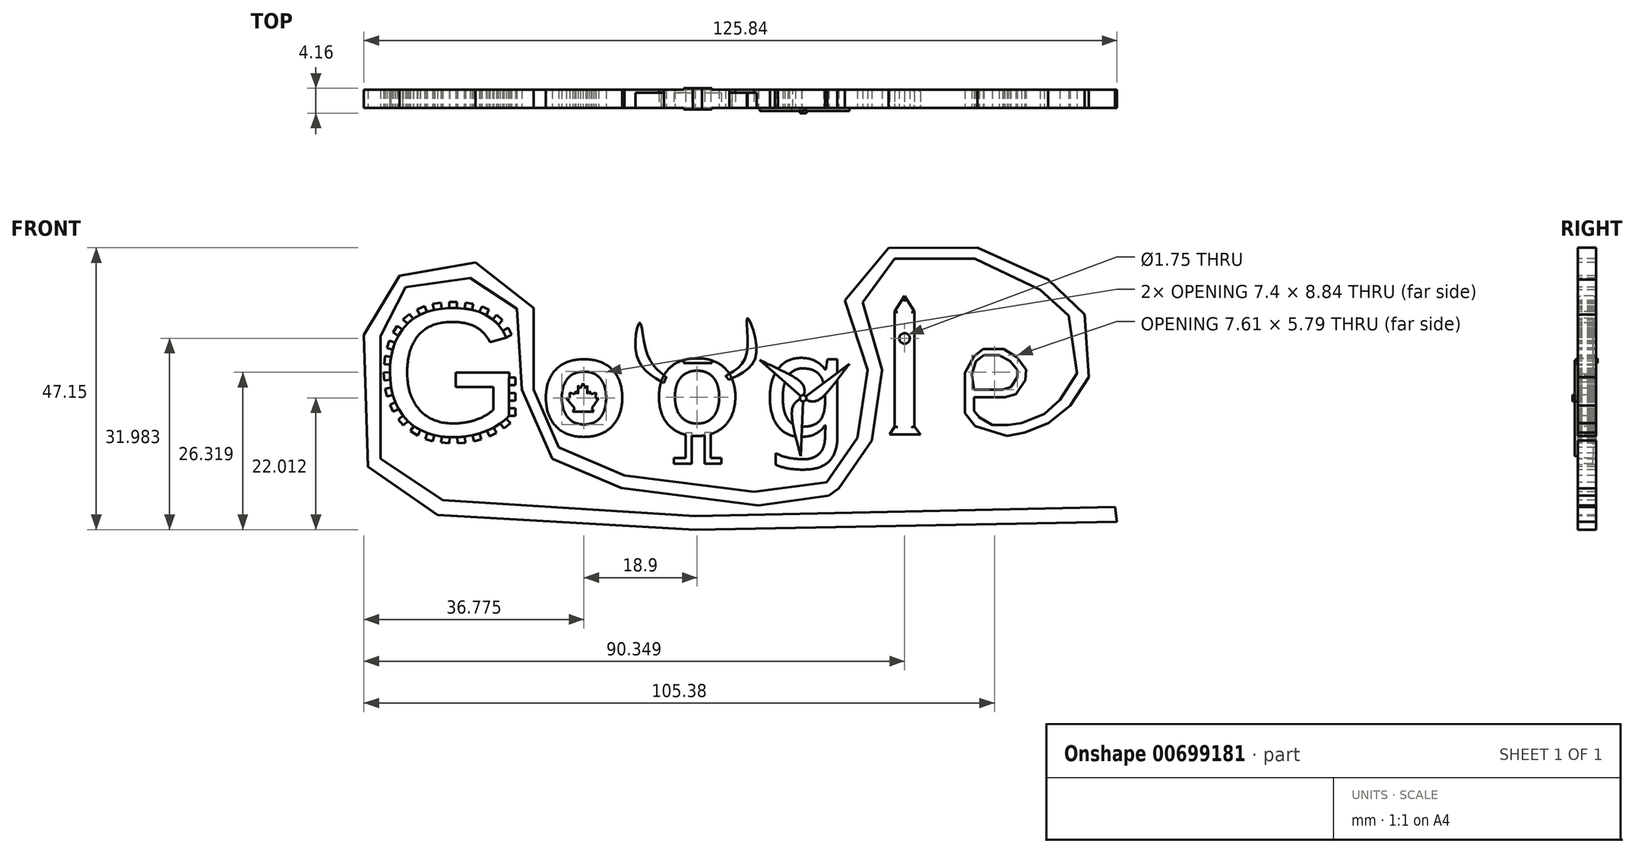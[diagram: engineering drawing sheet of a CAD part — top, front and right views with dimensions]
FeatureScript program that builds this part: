
annotation { "Feature Type Name" : "Feature", "Feature Type Description" : "" }
export const myFeature = defineFeature(function(context is Context, id is Id, definition is map)
    precondition{}
    {
        {
            var Q0;
            Q0=qCreatedBy(makeId("Front.planeOp"),FACE);
            var sketch = newSketch(context, id + "F0", { "sketchPlane" : qUnion([Q0])});
            skText(sketch, "E0", { "text": "G", "fontName": "Arimo-Regular.ttf"});
            skLineSegment(sketch, "E1", {"start": v(-51.76, 5.44) * mm, "end": v(-52.37, 6.57) * mm});
            skLineSegment(sketch, "E2", {"start": v(-52.37, 6.57) * mm, "end": v(-53.13, 7.6) * mm});
            skLineSegment(sketch, "E3", {"start": v(-53.13, 7.6) * mm, "end": v(-54.04, 8.49) * mm});
            skLineSegment(sketch, "E4", {"start": v(-54.04, 8.49) * mm, "end": v(-55.1, 9.2) * mm});
            skLineSegment(sketch, "E5", {"start": v(-55.1, 9.2) * mm, "end": v(-56.27, 9.71) * mm});
            skLineSegment(sketch, "E6", {"start": v(-56.27, 9.71) * mm, "end": v(-57.48, 10.05) * mm});
            skLineSegment(sketch, "E7", {"start": v(-57.48, 10.05) * mm, "end": v(-58.74, 10.26) * mm});
            skLineSegment(sketch, "E8", {"start": v(-58.74, 10.26) * mm, "end": v(-60, 10.36) * mm});
            skLineSegment(sketch, "E9", {"start": v(-60, 10.36) * mm, "end": v(-61.29, 10.36) * mm});
            skLineSegment(sketch, "E10", {"start": v(-61.29, 10.36) * mm, "end": v(-62.56, 10.28) * mm});
            skLineSegment(sketch, "E11", {"start": v(-62.56, 10.28) * mm, "end": v(-63.8, 10.08) * mm});
            skLineSegment(sketch, "E12", {"start": v(-63.8, 10.08) * mm, "end": v(-65.02, 9.73) * mm});
            skLineSegment(sketch, "E13", {"start": v(-65.02, 9.73) * mm, "end": v(-66.2, 9.24) * mm});
            skLineSegment(sketch, "E14", {"start": v(-66.2, 9.24) * mm, "end": v(-67.29, 8.59) * mm});
            skLineSegment(sketch, "E15", {"start": v(-67.29, 8.59) * mm, "end": v(-68.27, 7.77) * mm});
            skLineSegment(sketch, "E16", {"start": v(-68.27, 7.77) * mm, "end": v(-69.13, 6.82) * mm});
            skLineSegment(sketch, "E17", {"start": v(-69.13, 6.82) * mm, "end": v(-69.83, 5.76) * mm});
            skLineSegment(sketch, "E18", {"start": v(-69.83, 5.76) * mm, "end": v(-70.38, 4.62) * mm});
            skLineSegment(sketch, "E19", {"start": v(-70.38, 4.62) * mm, "end": v(-70.78, 3.41) * mm});
            skLineSegment(sketch, "E20", {"start": v(-70.78, 3.41) * mm, "end": v(-71.04, 2.16) * mm});
            skLineSegment(sketch, "E21", {"start": v(-71.04, 2.16) * mm, "end": v(-71.18, 0.9) * mm});
            skLineSegment(sketch, "E22", {"start": v(-71.18, 0.9) * mm, "end": v(-71.23, -0.38) * mm});
            skLineSegment(sketch, "E23", {"start": v(-71.23, -0.38) * mm, "end": v(-71.15, -1.65) * mm});
            skLineSegment(sketch, "E24", {"start": v(-71.15, -1.65) * mm, "end": v(-71.02, -2.92) * mm});
            skLineSegment(sketch, "E25", {"start": v(-71.02, -2.92) * mm, "end": v(-70.72, -4.17) * mm});
            skLineSegment(sketch, "E26", {"start": v(-70.72, -4.17) * mm, "end": v(-70.32, -5.38) * mm});
            skLineSegment(sketch, "E27", {"start": v(-70.32, -5.38) * mm, "end": v(-69.76, -6.52) * mm});
            skLineSegment(sketch, "E28", {"start": v(-69.76, -6.52) * mm, "end": v(-69.06, -7.58) * mm});
            skLineSegment(sketch, "E29", {"start": v(-69.06, -7.58) * mm, "end": v(-68.2, -8.53) * mm});
            skLineSegment(sketch, "E30", {"start": v(-68.2, -8.53) * mm, "end": v(-67.23, -9.34) * mm});
            skLineSegment(sketch, "E31", {"start": v(-67.23, -9.34) * mm, "end": v(-66.14, -10.01) * mm});
            skLineSegment(sketch, "E32", {"start": v(-66.14, -10.01) * mm, "end": v(-64.98, -10.53) * mm});
            skLineSegment(sketch, "E33", {"start": v(-64.98, -10.53) * mm, "end": v(-63.77, -10.9) * mm});
            skLineSegment(sketch, "E34", {"start": v(-63.77, -10.9) * mm, "end": v(-62.51, -11.12) * mm});
            skLineSegment(sketch, "E35", {"start": v(-62.51, -11.12) * mm, "end": v(-61.23, -11.21) * mm});
            skLineSegment(sketch, "E36", {"start": v(-61.23, -11.21) * mm, "end": v(-59.95, -11.21) * mm});
            skLineSegment(sketch, "E37", {"start": v(-59.95, -11.21) * mm, "end": v(-58.68, -11.13) * mm});
            skLineSegment(sketch, "E38", {"start": v(-58.68, -11.13) * mm, "end": v(-57.44, -10.9) * mm});
            skLineSegment(sketch, "E39", {"start": v(-57.44, -10.9) * mm, "end": v(-56.2, -10.6) * mm});
            skLineSegment(sketch, "E40", {"start": v(-56.2, -10.6) * mm, "end": v(-55, -10.15) * mm});
            skLineSegment(sketch, "E41", {"start": v(-55, -10.15) * mm, "end": v(-53.86, -9.6) * mm});
            skLineSegment(sketch, "E42", {"start": v(-53.86, -9.6) * mm, "end": v(-52.78, -8.93) * mm});
            skLineSegment(sketch, "E43", {"start": v(-52.78, -8.93) * mm, "end": v(-51.78, -8.14) * mm});
            skLineSegment(sketch, "E44", {"start": v(-51.78, -8.14) * mm, "end": v(-51.3, -7.67) * mm});
            skLineSegment(sketch, "E45", {"start": v(-51.3, -6.4) * mm, "end": v(-51.3, -5.1) * mm});
            skLineSegment(sketch, "E46", {"start": v(-51.3, -3.82) * mm, "end": v(-51.3, -2.54) * mm});
            skLineSegment(sketch, "E47", {"start": v(-51.3, -1.26) * mm, "end": v(-51.3, -0.43) * mm});
            skText(sketch, "E48", { "text": "O", "fontName": "Arimo-Bold.ttf"});
            skLineSegment(sketch, "E49", {"start": v(-38.96, -6.97) * mm, "end": v(-40.66, -6.97) * mm});
            skLineSegment(sketch, "E50", {"start": v(-40.66, -6.97) * mm, "end": v(-40.36, -6.4) * mm});
            skLineSegment(sketch, "E51", {"start": v(-40.36, -6.4) * mm, "end": v(-41.7, -4.7) * mm});
            skLineSegment(sketch, "E52", {"start": v(-41.7, -4.7) * mm, "end": v(-41.16, -4.7) * mm});
            skLineSegment(sketch, "E53", {"start": v(-41.16, -4.7) * mm, "end": v(-41.16, -3.75) * mm});
            skLineSegment(sketch, "E54", {"start": v(-41.16, -3.75) * mm, "end": v(-40.33, -4.05) * mm});
            skLineSegment(sketch, "E55", {"start": v(-40.33, -4.05) * mm, "end": v(-40.15, -3.53) * mm});
            skLineSegment(sketch, "E56", {"start": v(-40.15, -3.53) * mm, "end": v(-39.79, -3.99) * mm});
            skLineSegment(sketch, "E57", {"start": v(-39.79, -3.99) * mm, "end": v(-39.79, -2.56) * mm});
            skLineSegment(sketch, "E58", {"start": v(-39.79, -2.56) * mm, "end": v(-39.38, -3.07) * mm});
            skLineSegment(sketch, "E59", {"start": v(-39.38, -3.07) * mm, "end": v(-38.96, -2.2) * mm});
            skLineSegment(sketch, "E60", {"start": v(-38.96, -2.2) * mm, "end": v(-38.51, -3.07) * mm});
            skLineSegment(sketch, "E61", {"start": v(-38.51, -3.07) * mm, "end": v(-38.27, -2.56) * mm});
            skLineSegment(sketch, "E62", {"start": v(-38.27, -2.56) * mm, "end": v(-38.27, -3.99) * mm});
            skLineSegment(sketch, "E63", {"start": v(-38.27, -3.99) * mm, "end": v(-37.9, -3.53) * mm});
            skLineSegment(sketch, "E64", {"start": v(-37.9, -3.53) * mm, "end": v(-37.63, -4.05) * mm});
            skLineSegment(sketch, "E65", {"start": v(-37.63, -4.05) * mm, "end": v(-36.8, -3.75) * mm});
            skLineSegment(sketch, "E66", {"start": v(-36.8, -3.75) * mm, "end": v(-36.87, -4.7) * mm});
            skLineSegment(sketch, "E67", {"start": v(-36.87, -4.7) * mm, "end": v(-36.33, -4.7) * mm});
            skLineSegment(sketch, "E68", {"start": v(-36.33, -4.7) * mm, "end": v(-37.48, -6.4) * mm});
            skLineSegment(sketch, "E69", {"start": v(-37.48, -6.4) * mm, "end": v(-37.15, -6.97) * mm});
            skLineSegment(sketch, "E70", {"start": v(-37.15, -6.97) * mm, "end": v(-38.96, -6.97) * mm});
            skText(sketch, "E71", { "text": "O", "fontName": "Arimo-Bold.ttf"});
            skLineSegment(sketch, "E72.bottom", {"start": v(-22.1, 4.1) * mm, "end": v(-17.4, 4.1) * mm});
            skLineSegment(sketch, "E72.top", {"start": v(-22.1, 1.16) * mm, "end": v(-17.4, 1.16) * mm});
            skLineSegment(sketch, "E72.left", {"start": v(-22.1, 4.1) * mm, "end": v(-22.1, 1.16) * mm});
            skLineSegment(sketch, "E72.right", {"start": v(-17.4, 4.1) * mm, "end": v(-17.4, 1.16) * mm});
            skLineSegment(sketch, "E73.bottom", {"start": v(-20.6, 1.93) * mm, "end": v(-19.04, 1.93) * mm});
            skLineSegment(sketch, "E73.top", {"start": v(-20.6, 2.24) * mm, "end": v(-19.04, 2.24) * mm});
            skLineSegment(sketch, "E73.left", {"start": v(-20.6, 1.93) * mm, "end": v(-20.6, 2.24) * mm});
            skLineSegment(sketch, "E73.right", {"start": v(-19.04, 1.93) * mm, "end": v(-19.04, 2.24) * mm});
            skLineSegment(sketch, "E74", {"start": v(-20.45, 2.24) * mm, "end": v(-20.45, 1.93) * mm});
            skLineSegment(sketch, "E75", {"start": v(-20.28, 2.24) * mm, "end": v(-20.28, 1.93) * mm});
            skLineSegment(sketch, "E76", {"start": v(-20.12, 2.24) * mm, "end": v(-20.12, 1.93) * mm});
            skLineSegment(sketch, "E77", {"start": v(-19.98, 2.24) * mm, "end": v(-19.98, 1.93) * mm});
            skLineSegment(sketch, "E78", {"start": v(-19.82, 2.24) * mm, "end": v(-19.82, 1.93) * mm});
            skLineSegment(sketch, "E79", {"start": v(-19.66, 2.24) * mm, "end": v(-19.66, 1.93) * mm});
            skLineSegment(sketch, "E80", {"start": v(-19.5, 2.24) * mm, "end": v(-19.5, 1.93) * mm});
            skLineSegment(sketch, "E81", {"start": v(-19.36, 2.24) * mm, "end": v(-19.36, 1.93) * mm});
            skLineSegment(sketch, "E82", {"start": v(-19.2, 2.24) * mm, "end": v(-19.2, 1.93) * mm});
            skCircle(sketch, "E83", {"center": v(-20.99, 3.26) * mm, "radius": 0.6 * mm});
            skCircle(sketch, "E84", {"center": v(-18.95, 3.26) * mm, "radius": 0.6 * mm});
            skCircle(sketch, "E85", {"center": v(-19.92, 5.7) * mm, "radius": 0.2 * mm});
            skLineSegment(sketch, "E86", {"start": v(-19.92, 5.7) * mm, "end": v(-19.92, 4.1) * mm});
            skPoint(sketch, "E86.endSnap0", {"position": v(-19.75, 4.1) * mm});
            skText(sketch, "E87", { "text": "g", "fontName": "NotoSans-Regular.ttf"});
            skCircle(sketch, "E88", {"center": v(-2.16, -4.72) * mm, "radius": 0.53 * mm});
            skLineSegment(sketch, "E89", {"start": v(-2.16, -4.72) * mm, "end": v(5.58, 1.05) * mm});
            skFitSpline(sketch, "E90", {"points": [v(5.58, 1.05) * mm, v(0, -5.16) * mm, v(-2.16, -4.72) * mm], "startDerivative": vector(-11.92, -15.32) * mm, "endDerivative": vector(-6.32, 3.4) * mm});
            skLineSegment(sketch, "E91.bottom", {"start": v(-39.05, -6.97) * mm, "end": v(-38.88, -6.97) * mm});
            skLineSegment(sketch, "E91.top", {"start": v(-39.05, -8.07) * mm, "end": v(-38.88, -8.07) * mm});
            skLineSegment(sketch, "E91.left", {"start": v(-39.05, -6.97) * mm, "end": v(-39.05, -8.07) * mm});
            skLineSegment(sketch, "E91.right", {"start": v(-38.88, -6.97) * mm, "end": v(-38.88, -8.07) * mm});
            skLineSegment(sketch, "E92", {"start": v(-2.16, -4.72) * mm, "end": v(-9.4, 1.67) * mm});
            skLineSegment(sketch, "E93", {"start": v(-2.16, -4.72) * mm, "end": v(-2.58, -14.36) * mm});
            skFitSpline(sketch, "E94", {"points": [v(-2.58, -14.36) * mm, v(-3.88, -6.11) * mm, v(-2.16, -4.72) * mm], "startDerivative": vector(-4.21, 16.29) * mm, "endDerivative": vector(6.35, 1.11) * mm});
            skFitSpline(sketch, "E95", {"points": [v(-9.4, 1.67) * mm, v(-2.17, -2.5) * mm, v(-2.16, -4.72) * mm], "startDerivative": vector(13.96, -7.09) * mm, "endDerivative": vector(-1.69, -6.03) * mm});
            skLineSegment(sketch, "E96", {"start": v(-25, -1.2) * mm, "end": v(-25.49, -2.18) * mm});
            skLineSegment(sketch, "E97", {"start": v(-15.13, -0.99) * mm, "end": v(-14.56, -1.6) * mm});
            skFitSpline(sketch, "E98", {"points": [v(-25.49, -2.18) * mm, v(-30.03, 2.58) * mm, v(-29.46, 7.91) * mm, v(-28.22, 2.71) * mm, v(-25, -1.2) * mm], "startDerivative": vector(-22.02, 13.03) * mm, "endDerivative": vector(15.85, -12.09) * mm});
            skFitSpline(sketch, "E99", {"points": [v(-15.13, -0.99) * mm, v(-11.6, 2.71) * mm, v(-11.47, 8.66) * mm, v(-9.98, 2.71) * mm, v(-14.56, -1.6) * mm], "startDerivative": vector(19.64, 10.54) * mm, "endDerivative": vector(-24.7, -11.34) * mm});
            skLineSegment(sketch, "E100.bottom", {"start": v(-21.78, -10.46) * mm, "end": v(-20.78, -10.46) * mm});
            skLineSegment(sketch, "E100.top", {"start": v(-21.78, -15.64) * mm, "end": v(-20.78, -15.64) * mm});
            skLineSegment(sketch, "E100.left", {"start": v(-21.78, -10.46) * mm, "end": v(-21.78, -15.64) * mm});
            skLineSegment(sketch, "E100.right", {"start": v(-20.78, -10.46) * mm, "end": v(-20.78, -15.64) * mm});
            skLineSegment(sketch, "E101.bottom", {"start": v(-21.78, -15.64) * mm, "end": v(-23.74, -15.64) * mm});
            skLineSegment(sketch, "E101.top", {"start": v(-21.78, -14.7) * mm, "end": v(-23.74, -14.7) * mm});
            skLineSegment(sketch, "E101.left", {"start": v(-21.78, -15.64) * mm, "end": v(-21.78, -14.7) * mm});
            skLineSegment(sketch, "E101.right", {"start": v(-23.74, -15.64) * mm, "end": v(-23.74, -14.7) * mm});
            skLineSegment(sketch, "E102.bottom", {"start": v(-18.63, -10.4) * mm, "end": v(-17.63, -10.4) * mm});
            skLineSegment(sketch, "E102.top", {"start": v(-18.63, -15.64) * mm, "end": v(-17.63, -15.64) * mm});
            skLineSegment(sketch, "E102.left", {"start": v(-18.63, -10.4) * mm, "end": v(-18.63, -15.64) * mm});
            skLineSegment(sketch, "E102.right", {"start": v(-17.63, -10.4) * mm, "end": v(-17.63, -15.64) * mm});
            skLineSegment(sketch, "E103.bottom", {"start": v(-17.63, -15.64) * mm, "end": v(-15.83, -15.64) * mm});
            skLineSegment(sketch, "E103.top", {"start": v(-17.63, -14.7) * mm, "end": v(-15.83, -14.7) * mm});
            skLineSegment(sketch, "E103.left", {"start": v(-17.63, -15.64) * mm, "end": v(-17.63, -14.7) * mm});
            skLineSegment(sketch, "E103.right", {"start": v(-15.83, -15.64) * mm, "end": v(-15.83, -14.7) * mm});
            skLineSegment(sketch, "E104", {"start": v(-51.76, 5.44) * mm, "end": v(-50.87, 5.91) * mm});
            skLineSegment(sketch, "E105", {"start": v(-53.13, 7.6) * mm, "end": v(-52.42, 8.34) * mm});
            skLineSegment(sketch, "E106", {"start": v(-54.04, 8.49) * mm, "end": v(-53.34, 9.22) * mm});
            skLineSegment(sketch, "E107", {"start": v(-52.37, 6.57) * mm, "end": v(-51.48, 7.05) * mm});
            skLineSegment(sketch, "E108", {"start": v(-55.1, 9.2) * mm, "end": v(-54.7, 10.13) * mm});
            skLineSegment(sketch, "E109", {"start": v(-56.27, 9.71) * mm, "end": v(-55.86, 10.63) * mm});
            skLineSegment(sketch, "E110", {"start": v(-51.48, 7.05) * mm, "end": v(-50.87, 5.91) * mm});
            skLineSegment(sketch, "E111", {"start": v(-53.34, 9.22) * mm, "end": v(-52.42, 8.34) * mm});
            skLineSegment(sketch, "E112", {"start": v(-55.86, 10.63) * mm, "end": v(-54.7, 10.13) * mm});
            skLineSegment(sketch, "E113", {"start": v(-58.74, 10.26) * mm, "end": v(-58.56, 11.27) * mm});
            skLineSegment(sketch, "E114", {"start": v(-57.48, 10.05) * mm, "end": v(-57.31, 11.05) * mm});
            skLineSegment(sketch, "E115", {"start": v(-57.31, 11.05) * mm, "end": v(-58.56, 11.27) * mm});
            skLineSegment(sketch, "E116", {"start": v(-60, 10.36) * mm, "end": v(-60, 11.39) * mm});
            skLineSegment(sketch, "E117", {"start": v(-61.29, 10.36) * mm, "end": v(-61.29, 11.39) * mm});
            skLineSegment(sketch, "E118", {"start": v(-61.29, 11.39) * mm, "end": v(-60, 11.39) * mm});
            skLineSegment(sketch, "E119", {"start": v(-62.56, 10.28) * mm, "end": v(-62.72, 11.29) * mm});
            skLineSegment(sketch, "E120", {"start": v(-63.8, 10.08) * mm, "end": v(-64.08, 11.05) * mm});
            skLineSegment(sketch, "E121", {"start": v(-64.08, 11.05) * mm, "end": v(-62.72, 11.29) * mm});
            skLineSegment(sketch, "E122", {"start": v(-65.02, 9.73) * mm, "end": v(-65.41, 10.66) * mm});
            skLineSegment(sketch, "E123", {"start": v(-66.2, 9.24) * mm, "end": v(-66.7, 10.1) * mm});
            skLineSegment(sketch, "E124", {"start": v(-65.41, 10.66) * mm, "end": v(-66.7, 10.1) * mm});
            skLineSegment(sketch, "E125", {"start": v(-67.29, 8.59) * mm, "end": v(-67.95, 9.39) * mm});
            skLineSegment(sketch, "E126", {"start": v(-68.27, 7.77) * mm, "end": v(-69.03, 8.44) * mm});
            skLineSegment(sketch, "E127", {"start": v(-69.03, 8.44) * mm, "end": v(-67.95, 9.39) * mm});
            skLineSegment(sketch, "E128", {"start": v(-69.13, 6.82) * mm, "end": v(-69.98, 7.38) * mm});
            skLineSegment(sketch, "E129", {"start": v(-69.83, 5.76) * mm, "end": v(-70.68, 6.33) * mm});
            skLineSegment(sketch, "E130", {"start": v(-70.68, 6.33) * mm, "end": v(-69.98, 7.38) * mm});
            skLineSegment(sketch, "E131", {"start": v(-70.38, 4.62) * mm, "end": v(-71.34, 4.93) * mm});
            skLineSegment(sketch, "E132", {"start": v(-70.78, 3.41) * mm, "end": v(-71.73, 3.72) * mm});
            skLineSegment(sketch, "E133", {"start": v(-71.73, 3.72) * mm, "end": v(-71.34, 4.93) * mm});
            skLineSegment(sketch, "E134", {"start": v(-71.04, 2.16) * mm, "end": v(-72.04, 2.37) * mm});
            skLineSegment(sketch, "E135", {"start": v(-71.18, 0.9) * mm, "end": v(-72.18, 1.01) * mm});
            skLineSegment(sketch, "E136", {"start": v(-72.18, 1.01) * mm, "end": v(-72.04, 2.37) * mm});
            skLineSegment(sketch, "E137", {"start": v(-71.23, -0.38) * mm, "end": v(-72.26, -0.44) * mm});
            skLineSegment(sketch, "E138", {"start": v(-71.15, -1.65) * mm, "end": v(-72.16, -1.75) * mm});
            skLineSegment(sketch, "E139", {"start": v(-72.16, -1.75) * mm, "end": v(-72.26, -0.44) * mm});
            skLineSegment(sketch, "E140", {"start": v(-71.02, -2.92) * mm, "end": v(-72, -3.15) * mm});
            skLineSegment(sketch, "E141", {"start": v(-70.72, -4.17) * mm, "end": v(-71.72, -4.4) * mm});
            skLineSegment(sketch, "E142", {"start": v(-71.72, -4.4) * mm, "end": v(-72, -3.15) * mm});
            skLineSegment(sketch, "E143", {"start": v(-70.32, -5.38) * mm, "end": v(-71.23, -5.82) * mm});
            skLineSegment(sketch, "E144", {"start": v(-69.76, -6.52) * mm, "end": v(-70.68, -6.97) * mm});
            skLineSegment(sketch, "E145", {"start": v(-70.68, -6.97) * mm, "end": v(-71.23, -5.82) * mm});
            skLineSegment(sketch, "E146", {"start": v(-69.06, -7.58) * mm, "end": v(-69.82, -8.26) * mm});
            skLineSegment(sketch, "E147", {"start": v(-68.2, -8.53) * mm, "end": v(-68.97, -9.22) * mm});
            skLineSegment(sketch, "E148", {"start": v(-68.97, -9.22) * mm, "end": v(-69.82, -8.26) * mm});
            skLineSegment(sketch, "E149", {"start": v(-67.23, -9.34) * mm, "end": v(-67.77, -10.2) * mm});
            skLineSegment(sketch, "E150", {"start": v(-66.14, -10.01) * mm, "end": v(-66.56, -10.94) * mm});
            skLineSegment(sketch, "E151", {"start": v(-66.56, -10.94) * mm, "end": v(-67.77, -10.2) * mm});
            skLineSegment(sketch, "E152", {"start": v(-64.98, -10.53) * mm, "end": v(-65.28, -11.51) * mm});
            skLineSegment(sketch, "E153", {"start": v(-63.77, -10.9) * mm, "end": v(-64.07, -11.88) * mm});
            skLineSegment(sketch, "E154", {"start": v(-64.07, -11.88) * mm, "end": v(-65.28, -11.51) * mm});
            skLineSegment(sketch, "E155", {"start": v(-62.51, -11.12) * mm, "end": v(-62.69, -12.1) * mm});
            skLineSegment(sketch, "E156", {"start": v(-61.23, -11.21) * mm, "end": v(-61.31, -12.23) * mm});
            skLineSegment(sketch, "E157", {"start": v(-61.31, -12.23) * mm, "end": v(-62.69, -12.1) * mm});
            skLineSegment(sketch, "E158", {"start": v(-59.95, -11.21) * mm, "end": v(-59.88, -12.22) * mm});
            skLineSegment(sketch, "E159", {"start": v(-58.68, -11.13) * mm, "end": v(-58.62, -12.14) * mm});
            skLineSegment(sketch, "E160", {"start": v(-58.62, -12.14) * mm, "end": v(-59.88, -12.22) * mm});
            skLineSegment(sketch, "E161", {"start": v(-57.44, -10.9) * mm, "end": v(-57.2, -11.9) * mm});
            skLineSegment(sketch, "E162", {"start": v(-56.2, -10.6) * mm, "end": v(-55.96, -11.57) * mm});
            skLineSegment(sketch, "E163", {"start": v(-55.96, -11.57) * mm, "end": v(-57.2, -11.9) * mm});
            skLineSegment(sketch, "E164", {"start": v(-55, -10.15) * mm, "end": v(-54.57, -11.07) * mm});
            skLineSegment(sketch, "E165", {"start": v(-53.86, -9.6) * mm, "end": v(-53.42, -10.51) * mm});
            skLineSegment(sketch, "E166", {"start": v(-53.42, -10.51) * mm, "end": v(-54.57, -11.07) * mm});
            skLineSegment(sketch, "E167", {"start": v(-52.78, -8.93) * mm, "end": v(-52.14, -9.74) * mm});
            skLineSegment(sketch, "E168", {"start": v(-51.78, -8.14) * mm, "end": v(-51.08, -8.88) * mm});
            skLineSegment(sketch, "E169", {"start": v(-51.08, -8.88) * mm, "end": v(-52.14, -9.74) * mm});
            skLineSegment(sketch, "E170", {"start": v(-51.3, -7.67) * mm, "end": v(-50.27, -7.67) * mm});
            skLineSegment(sketch, "E171", {"start": v(-50.27, -7.67) * mm, "end": v(-50.27, -6.4) * mm});
            skLineSegment(sketch, "E172", {"start": v(-50.27, -6.4) * mm, "end": v(-51.3, -6.4) * mm});
            skLineSegment(sketch, "E173", {"start": v(-51.3, -5.1) * mm, "end": v(-50.27, -5.1) * mm});
            skLineSegment(sketch, "E174", {"start": v(-50.27, -5.1) * mm, "end": v(-50.27, -3.82) * mm});
            skLineSegment(sketch, "E175", {"start": v(-50.27, -3.82) * mm, "end": v(-51.3, -3.82) * mm});
            skLineSegment(sketch, "E176", {"start": v(-51.3, -2.54) * mm, "end": v(-50.27, -2.54) * mm});
            skLineSegment(sketch, "E177", {"start": v(-50.27, -2.54) * mm, "end": v(-50.27, -1.26) * mm});
            skLineSegment(sketch, "E178", {"start": v(-50.27, -1.26) * mm, "end": v(-51.3, -1.26) * mm});
            skLineSegment(sketch, "E179", {"start": v(-51.3, -1.26) * mm, "end": v(-51.3, -7.67) * mm});
            skLineSegment(sketch, "E180.bottom", {"start": v(13.14, 9.8) * mm, "end": v(16.44, 9.8) * mm});
            skLineSegment(sketch, "E180.top", {"start": v(13.14, -9.42) * mm, "end": v(16.44, -9.42) * mm});
            skLineSegment(sketch, "E180.left", {"start": v(13.14, 9.8) * mm, "end": v(13.14, -9.42) * mm});
            skLineSegment(sketch, "E180.right", {"start": v(16.44, 9.8) * mm, "end": v(16.44, -9.42) * mm});
            skLineSegment(sketch, "E181", {"start": v(14.79, 9.8) * mm, "end": v(14.79, 12.4) * mm});
            skLineSegment(sketch, "E182", {"start": v(14.79, 12.4) * mm, "end": v(13.14, 9.8) * mm});
            skLineSegment(sketch, "E183", {"start": v(16.44, 9.8) * mm, "end": v(14.79, 12.4) * mm});
            skLineSegment(sketch, "E184", {"start": v(13.14, -9.42) * mm, "end": v(12.3, -10.74) * mm});
            skLineSegment(sketch, "E185", {"start": v(12.3, -10.74) * mm, "end": v(16.44, -10.74) * mm});
            skLineSegment(sketch, "E186", {"start": v(16.44, -10.74) * mm, "end": v(16.44, -9.42) * mm});
            skLineSegment(sketch, "E187", {"start": v(16.44, -9.42) * mm, "end": v(17.47, -10.74) * mm});
            skLineSegment(sketch, "E188", {"start": v(17.47, -10.74) * mm, "end": v(16.44, -10.74) * mm});
            skCircle(sketch, "E189", {"center": v(14.79, 5.3) * mm, "radius": 0.88 * mm});
            skLineSegment(sketch, "E190", {"start": v(26.38, -4.4) * mm, "end": v(26.38, -3.27) * mm});
            skPoint(sketch, "E190.startSnap0", {"position": v(-38.51, -4.4) * mm});
            skLineSegment(sketch, "E191", {"start": v(26.38, -3.27) * mm, "end": v(31.17, -3.27) * mm});
            skLineSegment(sketch, "E192", {"start": v(31.17, -3.27) * mm, "end": v(32.56, -2.83) * mm});
            skLineSegment(sketch, "E193", {"start": v(32.56, -2.83) * mm, "end": v(33.63, -1.2) * mm});
            skLineSegment(sketch, "E194", {"start": v(33.63, -1.2) * mm, "end": v(33.63, 0) * mm});
            skLineSegment(sketch, "E195", {"start": v(33.63, 0) * mm, "end": v(32.46, 1.48) * mm});
            skLineSegment(sketch, "E196", {"start": v(32.46, 1.48) * mm, "end": v(30.6, 2.52) * mm});
            skLineSegment(sketch, "E197", {"start": v(30.6, 2.52) * mm, "end": v(28.03, 2.52) * mm});
            skLineSegment(sketch, "E198", {"start": v(28.03, 2.52) * mm, "end": v(26.7, 1.47) * mm});
            skLineSegment(sketch, "E199", {"start": v(26.7, 1.47) * mm, "end": v(26.01, -0.75) * mm});
            skLineSegment(sketch, "E200", {"start": v(26.01, -0.75) * mm, "end": v(26.38, -3.27) * mm});
            skLineSegment(sketch, "E201", {"start": v(26.4, -4.52) * mm, "end": v(26.4, -6.85) * mm});
            skLineSegment(sketch, "E202", {"start": v(26.4, -6.85) * mm, "end": v(27.31, -7.92) * mm});
            skLineSegment(sketch, "E203", {"start": v(27.31, -7.92) * mm, "end": v(29.47, -9.18) * mm});
            skLineSegment(sketch, "E204", {"start": v(29.47, -9.18) * mm, "end": v(32.12, -9.18) * mm});
            skLineSegment(sketch, "E205", {"start": v(32.12, -9.18) * mm, "end": v(34.32, -8.87) * mm});
            skLineSegment(sketch, "E206", {"start": v(26.4, -4.52) * mm, "end": v(31.55, -4.52) * mm});
            skLineSegment(sketch, "E207", {"start": v(31.55, -4.52) * mm, "end": v(33.38, -4.02) * mm});
            skLineSegment(sketch, "E208", {"start": v(33.38, -4.02) * mm, "end": v(34.95, -1.7) * mm});
            skLineSegment(sketch, "E209", {"start": v(34.95, -1.7) * mm, "end": v(35.07, 0.07) * mm});
            skLineSegment(sketch, "E210", {"start": v(35.07, 0.07) * mm, "end": v(33.5, 2.2) * mm});
            skLineSegment(sketch, "E211", {"start": v(33.5, 2.2) * mm, "end": v(31.36, 3.53) * mm});
            skLineSegment(sketch, "E212", {"start": v(31.36, 3.53) * mm, "end": v(27.9, 3.53) * mm});
            skLineSegment(sketch, "E213", {"start": v(27.9, 3.53) * mm, "end": v(26.4, 2.33) * mm});
            skLineSegment(sketch, "E214", {"start": v(26.4, 2.33) * mm, "end": v(24.88, -0.5) * mm});
            skLineSegment(sketch, "E215", {"start": v(24.88, -0.5) * mm, "end": v(24.88, -3.27) * mm});
            skLineSegment(sketch, "E216", {"start": v(24.88, -3.27) * mm, "end": v(24.88, -7.23) * mm});
            skLineSegment(sketch, "E217", {"start": v(24.88, -7.23) * mm, "end": v(26.58, -9.37) * mm});
            skLineSegment(sketch, "E218", {"start": v(26.58, -9.37) * mm, "end": v(29, -10.11) * mm});
            skLineSegment(sketch, "E219", {"start": v(29, -10.11) * mm, "end": v(31.94, -11) * mm});
            skLineSegment(sketch, "E220", {"start": v(31.94, -11) * mm, "end": v(34.82, -10.44) * mm});
            skLineSegment(sketch, "E221", {"start": v(34.82, -10.44) * mm, "end": v(38.85, -8.87) * mm});
            skLineSegment(sketch, "E222", {"start": v(38.85, -8.87) * mm, "end": v(42.44, -5.97) * mm});
            skLineSegment(sketch, "E223", {"start": v(42.44, -5.97) * mm, "end": v(45.58, -1.19) * mm});
            skLineSegment(sketch, "E224", {"start": v(45.58, -1.19) * mm, "end": v(44.9, 9.32) * mm});
            skLineSegment(sketch, "E225", {"start": v(44.9, 9.32) * mm, "end": v(38.79, 15.17) * mm});
            skLineSegment(sketch, "E226", {"start": v(38.79, 15.17) * mm, "end": v(26.96, 20.46) * mm});
            skLineSegment(sketch, "E227", {"start": v(26.96, 20.46) * mm, "end": v(12.1, 20.4) * mm});
            skLineSegment(sketch, "E228", {"start": v(12.1, 20.4) * mm, "end": v(4.8, 11.65) * mm});
            skLineSegment(sketch, "E229", {"start": v(4.8, 11.65) * mm, "end": v(8.64, 0) * mm});
            skLineSegment(sketch, "E230", {"start": v(8.64, 0) * mm, "end": v(6.88, -11.32) * mm});
            skLineSegment(sketch, "E231", {"start": v(6.88, -11.32) * mm, "end": v(1.78, -18.75) * mm});
            skLineSegment(sketch, "E232", {"start": v(1.78, -18.75) * mm, "end": v(-10.36, -20.38) * mm});
            skLineSegment(sketch, "E233", {"start": v(-10.36, -20.38) * mm, "end": v(-32.02, -17.62) * mm});
            skLineSegment(sketch, "E234", {"start": v(-32.02, -17.62) * mm, "end": v(-43, -12.94) * mm});
            skLineSegment(sketch, "E235", {"start": v(-43, -12.94) * mm, "end": v(-47.2, -3.27) * mm});
            skLineSegment(sketch, "E236", {"start": v(-47.2, -3.27) * mm, "end": v(-47.2, 10.36) * mm});
            skLineSegment(sketch, "E237", {"start": v(-47.2, 10.36) * mm, "end": v(-56.94, 18) * mm});
            skLineSegment(sketch, "E238", {"start": v(-56.94, 18) * mm, "end": v(-69.64, 15.8) * mm});
            skLineSegment(sketch, "E239", {"start": v(-69.64, 15.8) * mm, "end": v(-75.56, 5.87) * mm});
            skLineSegment(sketch, "E240", {"start": v(-75.56, 5.87) * mm, "end": v(-74.9, -16.19) * mm});
            skLineSegment(sketch, "E241", {"start": v(-74.9, -16.19) * mm, "end": v(-63.24, -24.2) * mm});
            skLineSegment(sketch, "E242", {"start": v(-63.24, -24.2) * mm, "end": v(-20.18, -26.69) * mm});
            skLineSegment(sketch, "E243", {"start": v(-20.18, -26.69) * mm, "end": v(50.28, -25.35) * mm});
            skLineSegment(sketch, "E244", {"start": v(34.32, -8.87) * mm, "end": v(38.15, -7.3) * mm});
            skLineSegment(sketch, "E245", {"start": v(38.15, -7.3) * mm, "end": v(40.73, -5.02) * mm});
            skLineSegment(sketch, "E246", {"start": v(40.73, -5.02) * mm, "end": v(43.6, -0.53) * mm});
            skLineSegment(sketch, "E247", {"start": v(43.6, -0.53) * mm, "end": v(42.22, 9.12) * mm});
            skLineSegment(sketch, "E248", {"start": v(42.22, 9.12) * mm, "end": v(37.48, 13.41) * mm});
            skLineSegment(sketch, "E249", {"start": v(37.48, 13.41) * mm, "end": v(26.5, 18.66) * mm});
            skLineSegment(sketch, "E250", {"start": v(26.5, 18.66) * mm, "end": v(13.14, 18.66) * mm});
            skLineSegment(sketch, "E251", {"start": v(13.14, 18.66) * mm, "end": v(7.8, 11.31) * mm});
            skLineSegment(sketch, "E252", {"start": v(7.8, 11.31) * mm, "end": v(11.04, 0) * mm});
            skLineSegment(sketch, "E253", {"start": v(11.04, 0) * mm, "end": v(9.32, -11.8) * mm});
            skLineSegment(sketch, "E254", {"start": v(9.32, -11.8) * mm, "end": v(3.78, -19.81) * mm});
            skLineSegment(sketch, "E255", {"start": v(3.78, -19.81) * mm, "end": v(2.16, -20.96) * mm});
            skLineSegment(sketch, "E256", {"start": v(2.16, -20.96) * mm, "end": v(-9.6, -22.64) * mm});
            skLineSegment(sketch, "E257", {"start": v(-9.6, -22.64) * mm, "end": v(-32.5, -19.72) * mm});
            skLineSegment(sketch, "E258", {"start": v(-32.5, -19.72) * mm, "end": v(-44.05, -14.85) * mm});
            skLineSegment(sketch, "E259", {"start": v(-44.05, -14.85) * mm, "end": v(-49.17, -3.3) * mm});
            skLineSegment(sketch, "E260", {"start": v(-49.17, -3.3) * mm, "end": v(-49.97, 10.26) * mm});
            skLineSegment(sketch, "E261", {"start": v(-49.97, 10.26) * mm, "end": v(-57.8, 15.42) * mm});
            skLineSegment(sketch, "E262", {"start": v(-57.8, 15.42) * mm, "end": v(-68.57, 13.88) * mm});
            skLineSegment(sketch, "E263", {"start": v(-68.57, 13.88) * mm, "end": v(-72.76, 5.68) * mm});
            skLineSegment(sketch, "E264", {"start": v(-72.76, 5.68) * mm, "end": v(-72.76, -14.85) * mm});
            skLineSegment(sketch, "E265", {"start": v(-72.76, -14.85) * mm, "end": v(-62.38, -21.72) * mm});
            skLineSegment(sketch, "E266", {"start": v(-62.38, -21.72) * mm, "end": v(-20.18, -24.4) * mm});
            skLineSegment(sketch, "E267", {"start": v(-20.18, -24.4) * mm, "end": v(50, -22.87) * mm});
            skLineSegment(sketch, "E268", {"start": v(50, -22.87) * mm, "end": v(50.28, -25.35) * mm});
            const initialGuessF0  = {"E0": [-0.07276, -0.01094, 1, 0, 0.02199], "E48": [-0.0459, -0.011, 1, 0, 0.01322], "E71": [-0.027, -0.01085, 1, 0, 0.01322], "E87": [-0.00903, -0.01094, 1, 0, 0.01711]};
            skSetInitialGuess(sketch, initialGuessF0);
            skSolve(sketch);
        }
        {
            var Q0;
            {var subQ98=sQuery(id+"F0.wireOp",EDGE,"E0.sketch_text.stroke-4");Q0=makeQuery(id+"F0.imprint","IMPRINT",FACE,{"disambiguationData":[TD([[makeQuery(id+"F0.imprint","IMPRINT",EDGE,{"derivedFrom":subQ98}),-1.0]])]});}
            var Q1;
            Q1=makeQuery(id+"F0.imprint","IMPRINT",FACE,{"disambiguationData":[TD([[makeQuery(id+"F0.imprint","IMPRINT",EDGE,{"derivedFrom":sQuery(id+"F0.wireOp",EDGE,"E48.sketch_text.stroke-0")}),-1.0]])]});
            var Q2;
            Q2=makeQuery(id+"F0.imprint","IMPRINT",FACE,{"disambiguationData":[TD([[makeQuery(id+"F0.imprint","IMPRINT",EDGE,{"derivedFrom":sQuery(id+"F0.wireOp",EDGE,"E71.sketch_text.stroke-0")}),-1.0]])]});
            var Q3;
            Q3=makeQuery(id+"F0.imprint","IMPRINT",FACE,{"disambiguationData":[TD([[makeQuery(id+"F0.imprint","IMPRINT",EDGE,{"derivedFrom":sQuery(id+"F0.wireOp",EDGE,"E87.sketch_text.stroke-0")}),-1.0]])]});
            extrude(context, id + "F1", {"entities" : qUnion([Q0, Q1, Q2, Q3]), "oppositeDirection" : true, "depth" : 3.05 * mm, "offsetDistance" : 25.4 * mm});
        }
        {
            var Q0;
            Q0=makeQuery(id+"F0.imprint","IMPRINT",FACE,{"disambiguationData":[TD([[makeQuery(id+"F0.imprint","IMPRINT",EDGE,{"derivedFrom":sQuery(id+"F0.wireOp",EDGE,"E49")}),-1.0]])]});
            var Q1;
            Q1=makeQuery(id+"F0.imprint","IMPRINT",FACE,{"disambiguationData":[TD([[makeQuery(id+"F0.imprint","IMPRINT",EDGE,{"derivedFrom":sQuery(id+"F0.wireOp",EDGE,"E91.bottom")}),-1.0]])]});
            extrude(context, id + "F2", {"entities" : qUnion([Q0, Q1]), "oppositeDirection" : true, "depth" : 3.05 * mm, "offsetDistance" : 25.4 * mm});
        }
        {
            var Q0;
            {var subQ0=sQuery(id+"F0.wireOp",EDGE,"E93");var subQ1=sQuery(id+"F0.wireOp",EDGE,"E88");var subQ2=makeQuery(id+"F0.imprint","INTERSECT",VERTEX,{"derivedFrom":[subQ1,subQ0]});Q0=makeQuery(id+"F0.imprint","IMPRINT",FACE,{"disambiguationData":[TD([[makeQuery(id+"F0.imprint","IMPRINT",EDGE,{"disambiguationData":[TD([[subQ2,-1.0]])],"derivedFrom":subQ1}),1.0]])]});}
            var Q1;
            {var subQ0=sQuery(id+"F0.wireOp",EDGE,"E89");var subQ1=sQuery(id+"F0.wireOp",EDGE,"E88");var subQ2=makeQuery(id+"F0.imprint","INTERSECT",VERTEX,{"derivedFrom":[subQ1,subQ0]});Q1=makeQuery(id+"F0.imprint","IMPRINT",FACE,{"disambiguationData":[TD([[makeQuery(id+"F0.imprint","IMPRINT",EDGE,{"disambiguationData":[TD([[subQ2,1.0]])],"derivedFrom":subQ1}),1.0]])]});}
            var Q2;
            {var subQ0=sQuery(id+"F0.wireOp",EDGE,"E95");var subQ1=sQuery(id+"F0.wireOp",EDGE,"E88");var subQ2=makeQuery(id+"F0.imprint","INTERSECT",VERTEX,{"derivedFrom":[subQ1,subQ0]});Q2=makeQuery(id+"F0.imprint","IMPRINT",FACE,{"disambiguationData":[TD([[makeQuery(id+"F0.imprint","IMPRINT",EDGE,{"disambiguationData":[TD([[subQ2,1.0]])],"derivedFrom":subQ1}),1.0]])]});}
            var Q3;
            {var subQ0=sQuery(id+"F0.wireOp",EDGE,"E95");var subQ1=sQuery(id+"F0.wireOp",EDGE,"E88");var subQ2=makeQuery(id+"F0.imprint","INTERSECT",VERTEX,{"derivedFrom":[subQ1,subQ0]});Q3=makeQuery(id+"F0.imprint","IMPRINT",FACE,{"disambiguationData":[TD([[makeQuery(id+"F0.imprint","IMPRINT",EDGE,{"disambiguationData":[TD([[subQ2,-1.0]])],"derivedFrom":subQ1}),1.0]])]});}
            var Q4;
            {var subQ0=sQuery(id+"F0.wireOp",EDGE,"E92");var subQ1=sQuery(id+"F0.wireOp",EDGE,"E88");var subQ2=makeQuery(id+"F0.imprint","INTERSECT",VERTEX,{"derivedFrom":[subQ1,subQ0]});Q4=makeQuery(id+"F0.imprint","IMPRINT",FACE,{"disambiguationData":[TD([[makeQuery(id+"F0.imprint","IMPRINT",EDGE,{"disambiguationData":[TD([[subQ2,-1.0]])],"derivedFrom":subQ1}),1.0]])]});}
            var Q5;
            {var subQ0=sQuery(id+"F0.wireOp",EDGE,"E94");var subQ1=sQuery(id+"F0.wireOp",EDGE,"E88");var subQ2=makeQuery(id+"F0.imprint","INTERSECT",VERTEX,{"derivedFrom":[subQ1,subQ0]});Q5=makeQuery(id+"F0.imprint","IMPRINT",FACE,{"disambiguationData":[TD([[makeQuery(id+"F0.imprint","IMPRINT",EDGE,{"disambiguationData":[TD([[subQ2,-1.0]])],"derivedFrom":subQ1}),1.0]])]});}
            extrude(context, id + "F3", {"entities" : qUnion([Q0, Q1, Q2, Q3, Q4, Q5]), "depth" : 0.86 * mm, "offsetDistance" : 25.4 * mm});
        }
        {
            var Q0;
            {var subQ5=sQuery(id+"F0.wireOp",EDGE,"E87.sketch_text.stroke-4");Q0=makeQuery(id+"F0.imprint","IMPRINT",FACE,{"disambiguationData":[TD([[makeQuery(id+"F0.imprint","IMPRINT",EDGE,{"derivedFrom":subQ5}),-1.0]])]});}
            var Q1;
            {var subQ1=sQuery(id+"F0.wireOp",EDGE,"E87.sketch_text.stroke-7");Q1=makeQuery(id+"F0.imprint","IMPRINT",FACE,{"disambiguationData":[TD([[makeQuery(id+"F0.imprint","IMPRINT",EDGE,{"derivedFrom":subQ1}),-1.0]])]});}
            extrude(context, id + "F4", {"entities" : qUnion([Q0, Q1]), "oppositeDirection" : true, "depth" : 3.05 * mm, "offsetDistance" : 25.4 * mm});
        }
        {
            var Q0;
            {var subQ0=sQuery(id+"F0.wireOp",EDGE,"E90");var subQ1=sQuery(id+"F0.wireOp",EDGE,"E87.sketch_text.stroke-3");var subQ2=makeQuery(id+"F0.imprint","INTERSECT",VERTEX,{"derivedFrom":[subQ1,subQ0]});Q0=makeQuery(id+"F0.imprint","IMPRINT",FACE,{"disambiguationData":[TD([[makeQuery(id+"F0.imprint","IMPRINT",EDGE,{"disambiguationData":[TD([[subQ2,-1.0]])],"derivedFrom":subQ1}),1.0]])]});}
            var Q1;
            {var subQ0=sQuery(id+"F0.wireOp",EDGE,"E90");var subQ1=sQuery(id+"F0.wireOp",EDGE,"E87.sketch_text.stroke-3");var subQ2=makeQuery(id+"F0.imprint","INTERSECT",VERTEX,{"derivedFrom":[subQ1,subQ0]});Q1=makeQuery(id+"F0.imprint","IMPRINT",FACE,{"disambiguationData":[TD([[makeQuery(id+"F0.imprint","IMPRINT",EDGE,{"disambiguationData":[TD([[subQ2,-1.0]])],"derivedFrom":subQ1}),-1.0]])]});}
            var Q2;
            {var subQ0=sQuery(id+"F0.wireOp",EDGE,"E89");var subQ1=sQuery(id+"F0.wireOp",EDGE,"E87.sketch_text.stroke-20");var subQ2=makeQuery(id+"F0.imprint","INTERSECT",VERTEX,{"derivedFrom":[subQ1,subQ0]});Q2=makeQuery(id+"F0.imprint","IMPRINT",FACE,{"disambiguationData":[TD([[makeQuery(id+"F0.imprint","IMPRINT",EDGE,{"disambiguationData":[TD([[subQ2,-1.0]])],"derivedFrom":subQ1}),1.0]])]});}
            var Q3;
            {var subQ0=sQuery(id+"F0.wireOp",EDGE,"E94");var subQ1=sQuery(id+"F0.wireOp",EDGE,"E87.sketch_text.stroke-8");var subQ2=makeQuery(id+"F0.imprint","INTERSECT",VERTEX,{"derivedFrom":[subQ1,subQ0]});Q3=makeQuery(id+"F0.imprint","IMPRINT",FACE,{"disambiguationData":[TD([[makeQuery(id+"F0.imprint","IMPRINT",EDGE,{"disambiguationData":[TD([[subQ2,-1.0]])],"derivedFrom":subQ1}),1.0]])]});}
            var Q4;
            {var subQ3=sQuery(id+"F0.wireOp",EDGE,"E87.sketch_text.stroke-8");var subQ7=sQuery(id+"F0.wireOp",EDGE,"E94");var subQ9=makeQuery(id+"F0.imprint","INTERSECT",VERTEX,{"derivedFrom":[subQ3,subQ7]});Q4=makeQuery(id+"F0.imprint","IMPRINT",FACE,{"disambiguationData":[TD([[makeQuery(id+"F0.imprint","IMPRINT",EDGE,{"disambiguationData":[TD([[subQ9,-1.0]])],"derivedFrom":subQ3}),-1.0]])]});}
            var Q5;
            {var subQ0=sQuery(id+"F0.wireOp",EDGE,"E87.sketch_text.stroke-12");var subQ1=sQuery(id+"F0.wireOp",EDGE,"E87.sketch_text.stroke-11");var subQ2=makeQuery(id+"F0.imprint","INTERSECT",VERTEX,{"derivedFrom":[subQ1,subQ0]});Q5=makeQuery(id+"F0.imprint","IMPRINT",FACE,{"disambiguationData":[TD([[makeQuery(id+"F0.imprint","IMPRINT",EDGE,{"disambiguationData":[TD([[subQ2,1.0]])],"derivedFrom":subQ1}),1.0]])]});}
            var Q6;
            {var subQ1=sQuery(id+"F0.wireOp",EDGE,"E87.sketch_text.stroke-6");var subQ7=sQuery(id+"F0.wireOp",EDGE,"E87.sketch_text.stroke-5");var subQ8=makeQuery(id+"F0.imprint","INTERSECT",VERTEX,{"derivedFrom":[subQ7,subQ1]});Q6=makeQuery(id+"F0.imprint","IMPRINT",FACE,{"disambiguationData":[TD([[makeQuery(id+"F0.imprint","IMPRINT",EDGE,{"disambiguationData":[TD([[subQ8,1.0]])],"derivedFrom":subQ7}),1.0]])]});}
            var Q7;
            {var subQ3=sQuery(id+"F0.wireOp",EDGE,"E87.sketch_text.stroke-6");var subQ7=sQuery(id+"F0.wireOp",EDGE,"E87.sketch_text.stroke-5");var subQ9=makeQuery(id+"F0.imprint","INTERSECT",VERTEX,{"derivedFrom":[subQ7,subQ3]});Q7=makeQuery(id+"F0.imprint","IMPRINT",FACE,{"disambiguationData":[TD([[makeQuery(id+"F0.imprint","IMPRINT",EDGE,{"disambiguationData":[TD([[subQ9,1.0]])],"derivedFrom":subQ7}),-1.0]])]});}
            var Q8;
            {var subQ0=sQuery(id+"F0.wireOp",EDGE,"E92");var subQ1=sQuery(id+"F0.wireOp",EDGE,"E87.sketch_text.stroke-14");var subQ2=makeQuery(id+"F0.imprint","INTERSECT",VERTEX,{"derivedFrom":[subQ1,subQ0]});Q8=makeQuery(id+"F0.imprint","IMPRINT",FACE,{"disambiguationData":[TD([[makeQuery(id+"F0.imprint","IMPRINT",EDGE,{"disambiguationData":[TD([[subQ2,-1.0]])],"derivedFrom":subQ1}),1.0]])]});}
            extrude(context, id + "F5", {"entities" : qUnion([Q0, Q1, Q2, Q3, Q4, Q5, Q6, Q7, Q8]), "operationType" : NewBodyOperationType.ADD, "depth" : 0.5 * mm, "offsetDistance" : 25.4 * mm});
        }
        {
            var Q0;
            {var subQ6=sQuery(id+"F0.wireOp",EDGE,"E73.right");Q0=makeQuery(id+"F0.imprint","IMPRINT",FACE,{"disambiguationData":[TD([[makeQuery(id+"F0.imprint","IMPRINT",EDGE,{"derivedFrom":subQ6}),-1.0]])]});}
            var Q1;
            {var subQ7=sQuery(id+"F0.wireOp",EDGE,"E72.top");Q1=makeQuery(id+"F0.imprint","IMPRINT",FACE,{"disambiguationData":[TD([[makeQuery(id+"F0.imprint","IMPRINT",EDGE,{"derivedFrom":subQ7}),1.0]])]});}
            extrude(context, id + "F6", {"entities" : qUnion([Q0, Q1]), "operationType" : NewBodyOperationType.ADD, "oppositeDirection" : true, "depth" : 3.3 * mm, "offsetDistance" : 25.4 * mm});
        }
        {
            var Q0;
            {var subQ6=sQuery(id+"F0.wireOp",EDGE,"E73.right");Q0=makeQuery(id+"F0.imprint","IMPRINT",FACE,{"disambiguationData":[TD([[makeQuery(id+"F0.imprint","IMPRINT",EDGE,{"derivedFrom":subQ6}),-1.0]])]});}
            var Q1;
            {var subQ7=sQuery(id+"F0.wireOp",EDGE,"E72.top");Q1=makeQuery(id+"F0.imprint","IMPRINT",FACE,{"disambiguationData":[TD([[makeQuery(id+"F0.imprint","IMPRINT",EDGE,{"derivedFrom":subQ7}),1.0]])]});}
            extrude(context, id + "F7", {"entities" : qUnion([Q0, Q1]), "operationType" : NewBodyOperationType.ADD, "depth" : 0.25 * mm, "offsetDistance" : 25.4 * mm});
        }
        {
            var Q0;
            {var subQ0=sQuery(id+"F0.wireOp",EDGE,"E98");var subQ1=sQuery(id+"F0.wireOp",EDGE,"E71.sketch_text.stroke-5");var subQ2=makeQuery(id+"F0.imprint","INTERSECT",VERTEX,{"disambiguationData":[OD(0.0)],"derivedFrom":[subQ1,subQ0]});Q0=makeQuery(id+"F0.imprint","IMPRINT",FACE,{"disambiguationData":[TD([[makeQuery(id+"F0.imprint","IMPRINT",EDGE,{"disambiguationData":[TD([[subQ2,-1.0]])],"derivedFrom":subQ1}),1.0]])]});}
            var Q1;
            {var subQ0=sQuery(id+"F0.wireOp",EDGE,"E99");var subQ1=sQuery(id+"F0.wireOp",EDGE,"E71.sketch_text.stroke-8");var subQ2=makeQuery(id+"F0.imprint","INTERSECT",VERTEX,{"disambiguationData":[OD(0.0)],"derivedFrom":[subQ1,subQ0]});Q1=makeQuery(id+"F0.imprint","IMPRINT",FACE,{"disambiguationData":[TD([[makeQuery(id+"F0.imprint","IMPRINT",EDGE,{"disambiguationData":[TD([[subQ2,-1.0]])],"derivedFrom":subQ1}),1.0]])]});}
            extrude(context, id + "F8", {"entities" : qUnion([Q0, Q1]), "oppositeDirection" : true, "depth" : 2.54 * mm, "offsetDistance" : 25.4 * mm});
        }
        {
            var Q0;
            {var subQ4=sQuery(id+"F0.wireOp",EDGE,"E96");Q0=makeQuery(id+"F0.imprint","IMPRINT",FACE,{"disambiguationData":[TD([[makeQuery(id+"F0.imprint","IMPRINT",EDGE,{"derivedFrom":subQ4}),-1.0]])]});}
            var Q1;
            {var subQ4=sQuery(id+"F0.wireOp",EDGE,"E97");Q1=makeQuery(id+"F0.imprint","IMPRINT",FACE,{"disambiguationData":[TD([[makeQuery(id+"F0.imprint","IMPRINT",EDGE,{"derivedFrom":subQ4}),1.0]])]});}
            extrude(context, id + "F9", {"entities" : qUnion([Q0, Q1]), "oppositeDirection" : true, "depth" : 3.05 * mm, "offsetDistance" : 25.4 * mm});
        }
        {
            var Q0;
            {var subQ1=sQuery(id+"F0.wireOp",EDGE,"E100.top");Q0=makeQuery(id+"F0.imprint","IMPRINT",FACE,{"disambiguationData":[TD([[makeQuery(id+"F0.imprint","IMPRINT",EDGE,{"derivedFrom":subQ1}),1.0]])]});}
            var Q1;
            {var subQ1=sQuery(id+"F0.wireOp",EDGE,"E102.top");Q1=makeQuery(id+"F0.imprint","IMPRINT",FACE,{"disambiguationData":[TD([[makeQuery(id+"F0.imprint","IMPRINT",EDGE,{"derivedFrom":subQ1}),1.0]])]});}
            var Q2;
            {var subQ5=sQuery(id+"F0.wireOp",EDGE,"E100.bottom");Q2=makeQuery(id+"F0.imprint","IMPRINT",FACE,{"disambiguationData":[TD([[makeQuery(id+"F0.imprint","IMPRINT",EDGE,{"derivedFrom":subQ5}),-1.0]])]});}
            var Q3;
            {var subQ5=sQuery(id+"F0.wireOp",EDGE,"E102.bottom");Q3=makeQuery(id+"F0.imprint","IMPRINT",FACE,{"disambiguationData":[TD([[makeQuery(id+"F0.imprint","IMPRINT",EDGE,{"derivedFrom":subQ5}),-1.0]])]});}
            var Q4;
            Q4=makeQuery(id+"F0.imprint","IMPRINT",FACE,{"disambiguationData":[TD([[makeQuery(id+"F0.imprint","IMPRINT",EDGE,{"derivedFrom":sQuery(id+"F0.wireOp",EDGE,"E103.bottom")}),1.0]])]});
            var Q5;
            Q5=makeQuery(id+"F0.imprint","IMPRINT",FACE,{"disambiguationData":[TD([[makeQuery(id+"F0.imprint","IMPRINT",EDGE,{"derivedFrom":sQuery(id+"F0.wireOp",EDGE,"E101.bottom")}),-1.0]])]});
            extrude(context, id + "F10", {"entities" : qUnion([Q0, Q1, Q2, Q3, Q4, Q5]), "operationType" : NewBodyOperationType.ADD, "oppositeDirection" : true, "depth" : 2.54 * mm, "offsetDistance" : 25.4 * mm});
        }
        {
            var Q0;
            {var subQ5=sQuery(id+"F0.wireOp",EDGE,"E110");Q0=makeQuery(id+"F0.imprint","IMPRINT",FACE,{"disambiguationData":[TD([[makeQuery(id+"F0.imprint","IMPRINT",EDGE,{"derivedFrom":subQ5}),-1.0]])]});}
            var Q1;
            {var subQ5=sQuery(id+"F0.wireOp",EDGE,"E111");Q1=makeQuery(id+"F0.imprint","IMPRINT",FACE,{"disambiguationData":[TD([[makeQuery(id+"F0.imprint","IMPRINT",EDGE,{"derivedFrom":subQ5}),-1.0]])]});}
            var Q2;
            {var subQ0=sQuery(id+"F0.wireOp",EDGE,"E112");Q2=makeQuery(id+"F0.imprint","IMPRINT",FACE,{"disambiguationData":[TD([[makeQuery(id+"F0.imprint","IMPRINT",EDGE,{"derivedFrom":subQ0}),-1.0]])]});}
            var Q3;
            {var subQ5=sQuery(id+"F0.wireOp",EDGE,"E115");Q3=makeQuery(id+"F0.imprint","IMPRINT",FACE,{"disambiguationData":[TD([[makeQuery(id+"F0.imprint","IMPRINT",EDGE,{"derivedFrom":subQ5}),1.0]])]});}
            var Q4;
            {var subQ0=sQuery(id+"F0.wireOp",EDGE,"E118");Q4=makeQuery(id+"F0.imprint","IMPRINT",FACE,{"disambiguationData":[TD([[makeQuery(id+"F0.imprint","IMPRINT",EDGE,{"derivedFrom":subQ0}),-1.0]])]});}
            var Q5;
            {var subQ0=sQuery(id+"F0.wireOp",EDGE,"E120");Q5=makeQuery(id+"F0.imprint","IMPRINT",FACE,{"disambiguationData":[TD([[makeQuery(id+"F0.imprint","IMPRINT",EDGE,{"derivedFrom":subQ0}),-1.0]])]});}
            var Q6;
            {var subQ5=sQuery(id+"F0.wireOp",EDGE,"E127");Q6=makeQuery(id+"F0.imprint","IMPRINT",FACE,{"disambiguationData":[TD([[makeQuery(id+"F0.imprint","IMPRINT",EDGE,{"derivedFrom":subQ5}),-1.0]])]});}
            var Q7;
            {var subQ5=sQuery(id+"F0.wireOp",EDGE,"E130");Q7=makeQuery(id+"F0.imprint","IMPRINT",FACE,{"disambiguationData":[TD([[makeQuery(id+"F0.imprint","IMPRINT",EDGE,{"derivedFrom":subQ5}),-1.0]])]});}
            var Q8;
            {var subQ5=sQuery(id+"F0.wireOp",EDGE,"E133");Q8=makeQuery(id+"F0.imprint","IMPRINT",FACE,{"disambiguationData":[TD([[makeQuery(id+"F0.imprint","IMPRINT",EDGE,{"derivedFrom":subQ5}),-1.0]])]});}
            var Q9;
            {var subQ5=sQuery(id+"F0.wireOp",EDGE,"E136");Q9=makeQuery(id+"F0.imprint","IMPRINT",FACE,{"disambiguationData":[TD([[makeQuery(id+"F0.imprint","IMPRINT",EDGE,{"derivedFrom":subQ5}),-1.0]])]});}
            var Q10;
            {var subQ0=sQuery(id+"F0.wireOp",EDGE,"E137");Q10=makeQuery(id+"F0.imprint","IMPRINT",FACE,{"disambiguationData":[TD([[makeQuery(id+"F0.imprint","IMPRINT",EDGE,{"derivedFrom":subQ0}),1.0]])]});}
            var Q11;
            {var subQ5=sQuery(id+"F0.wireOp",EDGE,"E124");Q11=makeQuery(id+"F0.imprint","IMPRINT",FACE,{"disambiguationData":[TD([[makeQuery(id+"F0.imprint","IMPRINT",EDGE,{"derivedFrom":subQ5}),1.0]])]});}
            var Q12;
            {var subQ5=sQuery(id+"F0.wireOp",EDGE,"E142");Q12=makeQuery(id+"F0.imprint","IMPRINT",FACE,{"disambiguationData":[TD([[makeQuery(id+"F0.imprint","IMPRINT",EDGE,{"derivedFrom":subQ5}),-1.0]])]});}
            var Q13;
            {var subQ0=sQuery(id+"F0.wireOp",EDGE,"E145");Q13=makeQuery(id+"F0.imprint","IMPRINT",FACE,{"disambiguationData":[TD([[makeQuery(id+"F0.imprint","IMPRINT",EDGE,{"derivedFrom":subQ0}),-1.0]])]});}
            var Q14;
            {var subQ5=sQuery(id+"F0.wireOp",EDGE,"E148");Q14=makeQuery(id+"F0.imprint","IMPRINT",FACE,{"disambiguationData":[TD([[makeQuery(id+"F0.imprint","IMPRINT",EDGE,{"derivedFrom":subQ5}),-1.0]])]});}
            var Q15;
            {var subQ0=sQuery(id+"F0.wireOp",EDGE,"E151");Q15=makeQuery(id+"F0.imprint","IMPRINT",FACE,{"disambiguationData":[TD([[makeQuery(id+"F0.imprint","IMPRINT",EDGE,{"derivedFrom":subQ0}),-1.0]])]});}
            var Q16;
            {var subQ0=sQuery(id+"F0.wireOp",EDGE,"E153");Q16=makeQuery(id+"F0.imprint","IMPRINT",FACE,{"disambiguationData":[TD([[makeQuery(id+"F0.imprint","IMPRINT",EDGE,{"derivedFrom":subQ0}),-1.0]])]});}
            var Q17;
            {var subQ5=sQuery(id+"F0.wireOp",EDGE,"E157");Q17=makeQuery(id+"F0.imprint","IMPRINT",FACE,{"disambiguationData":[TD([[makeQuery(id+"F0.imprint","IMPRINT",EDGE,{"derivedFrom":subQ5}),-1.0]])]});}
            var Q18;
            {var subQ5=sQuery(id+"F0.wireOp",EDGE,"E166");Q18=makeQuery(id+"F0.imprint","IMPRINT",FACE,{"disambiguationData":[TD([[makeQuery(id+"F0.imprint","IMPRINT",EDGE,{"derivedFrom":subQ5}),-1.0]])]});}
            var Q19;
            {var subQ5=sQuery(id+"F0.wireOp",EDGE,"E163");Q19=makeQuery(id+"F0.imprint","IMPRINT",FACE,{"disambiguationData":[TD([[makeQuery(id+"F0.imprint","IMPRINT",EDGE,{"derivedFrom":subQ5}),-1.0]])]});}
            var Q20;
            {var subQ4=sQuery(id+"F0.wireOp",EDGE,"E159");Q20=makeQuery(id+"F0.imprint","IMPRINT",FACE,{"disambiguationData":[TD([[makeQuery(id+"F0.imprint","IMPRINT",EDGE,{"derivedFrom":subQ4}),-1.0]])]});}
            extrude(context, id + "F11", {"entities" : qUnion([Q0, Q1, Q2, Q3, Q4, Q5, Q6, Q7, Q8, Q9, Q10, Q11, Q12, Q13, Q14, Q15, Q16, Q17, Q18, Q19, Q20]), "oppositeDirection" : true, "depth" : 3.05 * mm, "offsetDistance" : 25.4 * mm});
        }
        {
            var Q0;
            {var subQ0=sQuery(id+"F0.wireOp",EDGE,"E170");Q0=makeQuery(id+"F0.imprint","IMPRINT",FACE,{"disambiguationData":[TD([[makeQuery(id+"F0.imprint","IMPRINT",EDGE,{"derivedFrom":subQ0}),1.0]])]});}
            var Q1;
            {var subQ0=sQuery(id+"F0.wireOp",EDGE,"E173");Q1=makeQuery(id+"F0.imprint","IMPRINT",FACE,{"disambiguationData":[TD([[makeQuery(id+"F0.imprint","IMPRINT",EDGE,{"derivedFrom":subQ0}),1.0]])]});}
            var Q2;
            {var subQ0=sQuery(id+"F0.wireOp",EDGE,"E176");Q2=makeQuery(id+"F0.imprint","IMPRINT",FACE,{"disambiguationData":[TD([[makeQuery(id+"F0.imprint","IMPRINT",EDGE,{"derivedFrom":subQ0}),1.0]])]});}
            extrude(context, id + "F12", {"entities" : qUnion([Q0, Q1, Q2]), "oppositeDirection" : true, "depth" : 3.05 * mm, "offsetDistance" : 25.4 * mm});
        }
        {
            var Q0;
            {var subQ5=sQuery(id+"F0.wireOp",EDGE,"E169");Q0=makeQuery(id+"F0.imprint","IMPRINT",FACE,{"disambiguationData":[TD([[makeQuery(id+"F0.imprint","IMPRINT",EDGE,{"derivedFrom":subQ5}),-1.0]])]});}
            extrude(context, id + "F13", {"entities" : qUnion([Q0]), "oppositeDirection" : true, "depth" : 3.05 * mm, "offsetDistance" : 25.4 * mm});
        }
        {
            var Q0;
            {var subQ2=sQuery(id+"F0.wireOp",EDGE,"E181");Q0=makeQuery(id+"F0.imprint","IMPRINT",FACE,{"disambiguationData":[TD([[makeQuery(id+"F0.imprint","IMPRINT",EDGE,{"derivedFrom":subQ2}),1.0]])]});}
            var Q1;
            {var subQ2=sQuery(id+"F0.wireOp",EDGE,"E181");Q1=makeQuery(id+"F0.imprint","IMPRINT",FACE,{"disambiguationData":[TD([[makeQuery(id+"F0.imprint","IMPRINT",EDGE,{"derivedFrom":subQ2}),-1.0]])]});}
            var Q2;
            Q2=makeQuery(id+"F0.imprint","IMPRINT",FACE,{"disambiguationData":[TD([[makeQuery(id+"F0.imprint","IMPRINT",EDGE,{"derivedFrom":sQuery(id+"F0.wireOp",EDGE,"E180.top")}),1.0]])]});
            var Q3;
            Q3=makeQuery(id+"F0.imprint","IMPRINT",FACE,{"disambiguationData":[TD([[makeQuery(id+"F0.imprint","IMPRINT",EDGE,{"derivedFrom":sQuery(id+"F0.wireOp",EDGE,"E180.top")}),-1.0]])]});
            var Q4;
            Q4=makeQuery(id+"F0.imprint","IMPRINT",FACE,{"disambiguationData":[TD([[makeQuery(id+"F0.imprint","IMPRINT",EDGE,{"derivedFrom":sQuery(id+"F0.wireOp",EDGE,"E186")}),-1.0]])]});
            extrude(context, id + "F14", {"entities" : qUnion([Q0, Q1, Q2, Q3, Q4]), "oppositeDirection" : true, "depth" : 3.05 * mm, "offsetDistance" : 25.4 * mm});
        }
        {
            var Q0;
            Q0=makeQuery(id+"F14.opExtrude","CAP_EDGE",EDGE,{"disambiguationData":[OSD([sQuery(id+"F0.wireOp",EDGE,"E180.right")])],"isStart":true});
            var Q1;
            Q1=makeQuery(id+"F14.opExtrude","CAP_EDGE",EDGE,{"disambiguationData":[OSD([sQuery(id+"F0.wireOp",EDGE,"E187")])],"isStart":true});
            var Q2;
            Q2=makeQuery(id+"F14.opExtrude","CAP_EDGE",EDGE,{"disambiguationData":[OSD([sQuery(id+"F0.wireOp",EDGE,"E184")])],"isStart":true});
            var Q3;
            Q3=makeQuery(id+"F14.opExtrude","CAP_EDGE",EDGE,{"disambiguationData":[OSD([sQuery(id+"F0.wireOp",EDGE,"E180.left")])],"isStart":true});
            var Q4;
            Q4=makeQuery(id+"F14.opExtrude","CAP_EDGE",EDGE,{"disambiguationData":[OSD([sQuery(id+"F0.wireOp",EDGE,"E182")])],"isStart":true});
            var Q5;
            Q5=makeQuery(id+"F14.opExtrude","CAP_EDGE",EDGE,{"disambiguationData":[OSD([sQuery(id+"F0.wireOp",EDGE,"E183")])],"isStart":true});
            var Q6;
            Q6=makeQuery(id+"F14.opExtrude","CAP_EDGE",EDGE,{"disambiguationData":[OSD([sQuery(id+"F0.wireOp",EDGE,"E180.left")])],"isStart":false});
            var Q7;
            Q7=makeQuery(id+"F14.opExtrude","CAP_EDGE",EDGE,{"disambiguationData":[OSD([sQuery(id+"F0.wireOp",EDGE,"E180.right")])],"isStart":false});
            var Q8;
            Q8=makeQuery(id+"F14.opExtrude","CAP_EDGE",EDGE,{"disambiguationData":[OSD([sQuery(id+"F0.wireOp",EDGE,"E183")])],"isStart":false});
            var Q9;
            Q9=makeQuery(id+"F14.opExtrude","CAP_EDGE",EDGE,{"disambiguationData":[OSD([sQuery(id+"F0.wireOp",EDGE,"E187")])],"isStart":false});
            var Q10;
            Q10=makeQuery(id+"F14.opExtrude","CAP_EDGE",EDGE,{"disambiguationData":[OSD([sQuery(id+"F0.wireOp",EDGE,"E184")])],"isStart":false});
            var Q11;
            Q11=makeQuery(id+"F14.opExtrude","CAP_EDGE",EDGE,{"disambiguationData":[OSD([sQuery(id+"F0.wireOp",EDGE,"E182")])],"isStart":false});
            fillet(context, id + "F15", {"entities" : qUnion([Q0, Q1, Q2, Q3, Q4, Q5, Q6, Q7, Q8, Q9, Q10, Q11]), "radius" : 0.5 * mm, "tangentPropagation" : true, "allowEdgeOverflow" : false});
        }
        {
            var Q0;
            Q0=makeQuery(id+"F0.imprint","IMPRINT",FACE,{"disambiguationData":[TD([[makeQuery(id+"F0.imprint","IMPRINT",EDGE,{"derivedFrom":sQuery(id+"F0.wireOp",EDGE,"E191")}),-1.0]])]});
            extrude(context, id + "F16", {"entities" : qUnion([Q0]), "oppositeDirection" : true, "depth" : 3.05 * mm, "offsetDistance" : 25.4 * mm});
        }
    });
